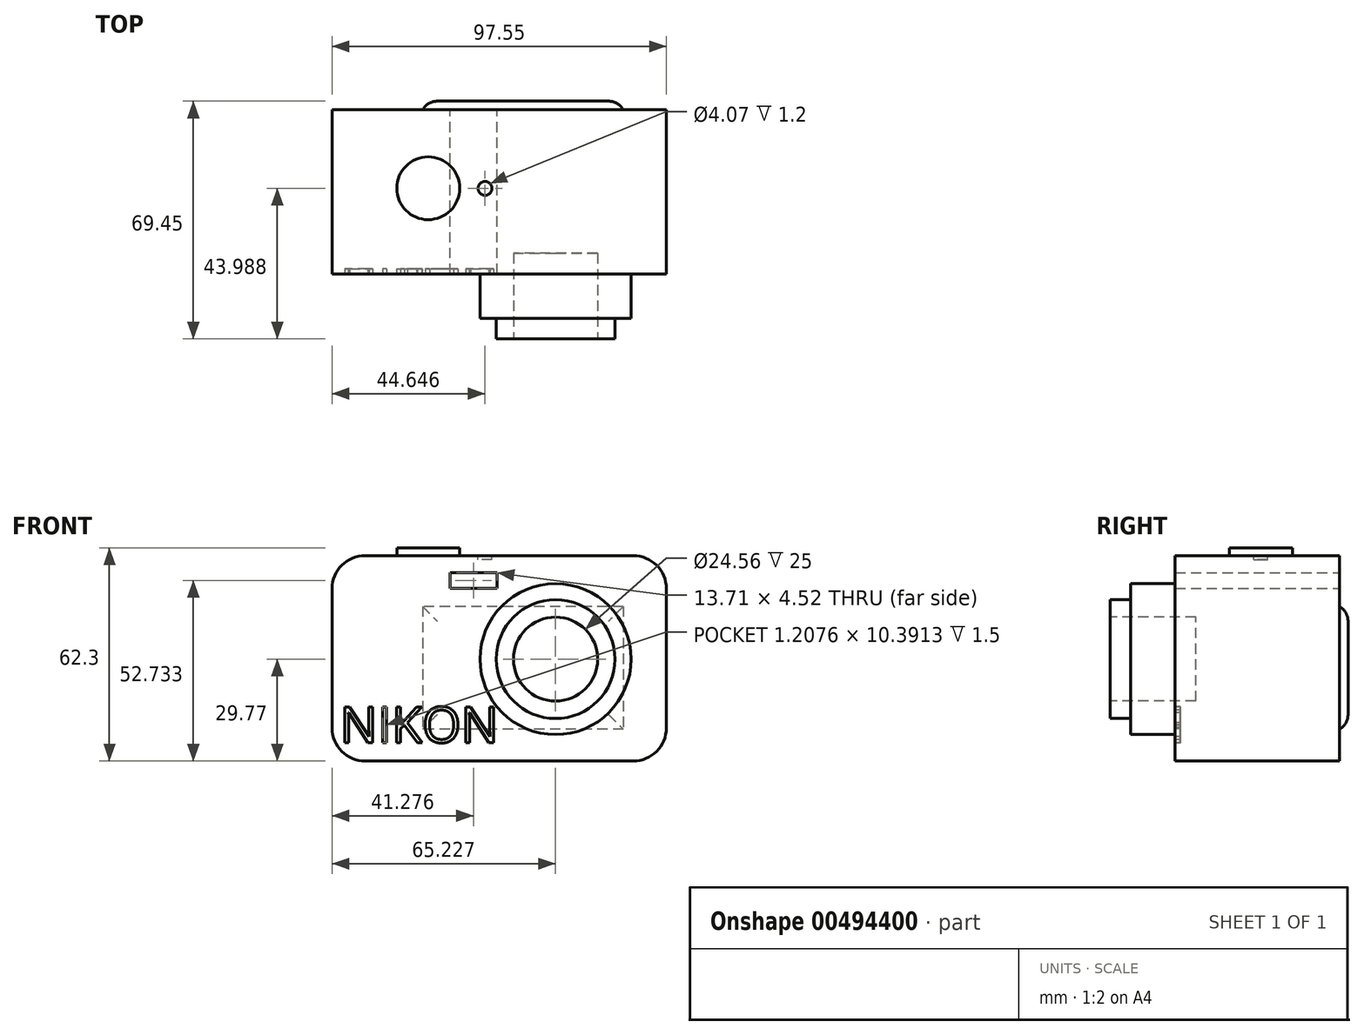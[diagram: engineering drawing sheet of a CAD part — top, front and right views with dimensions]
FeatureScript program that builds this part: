
annotation { "Feature Type Name" : "Feature", "Feature Type Description" : "" }
export const myFeature = defineFeature(function(context is Context, id is Id, definition is map)
    precondition{}
    {
        {
            var Q0;
            Q0=qCreatedBy(makeId("Top.planeOp"),FACE);
            var sketch = newSketch(context, id + "F0", { "sketchPlane" : qUnion([Q0])});
            skLineSegment(sketch, "E0.bottom", {"start": v(-58.63, 22.98) * mm, "end": v(38.92, 22.98) * mm});
            skLineSegment(sketch, "E0.top", {"start": v(-58.63, -24.97) * mm, "end": v(38.92, -24.97) * mm});
            skLineSegment(sketch, "E0.left", {"start": v(-58.63, 22.98) * mm, "end": v(-58.63, -24.97) * mm});
            skLineSegment(sketch, "E0.right", {"start": v(38.92, 22.98) * mm, "end": v(38.92, -24.97) * mm});
            skSolve(sketch);
        }
        {
            var Q0;
            Q0 = qSketchRegion(id + "F0", true);
            extrude(context, id + "F1", {"entities" : qUnion([Q0]), "depth" : 60 * mm});
        }
        {
            var Q0;
            Q0=makeQuery(id+"F1.opExtrude","CAP_EDGE",EDGE,{"disambiguationData":[OSD([sQuery(id+"F0.wireOp",EDGE,"E0.right")])],"isStart":false});
            var Q1;
            Q1=makeQuery(id+"F1.opExtrude","CAP_EDGE",EDGE,{"disambiguationData":[OSD([sQuery(id+"F0.wireOp",EDGE,"E0.left")])],"isStart":false});
            var Q2;
            Q2=makeQuery(id+"F1.opExtrude","CAP_EDGE",EDGE,{"disambiguationData":[OSD([sQuery(id+"F0.wireOp",EDGE,"E0.right")])],"isStart":true});
            var Q3;
            Q3=makeQuery(id+"F1.opExtrude","CAP_EDGE",EDGE,{"disambiguationData":[OSD([sQuery(id+"F0.wireOp",EDGE,"E0.left")])],"isStart":true});
            fillet(context, id + "F2", {"entities" : qUnion([Q0, Q1, Q2, Q3]), "radius" : 9.66 * mm, "tangentPropagation" : true, "allowEdgeOverflow" : false});
        }
        {
            var Q0;
            Q0=makeQuery(id+"F1.opExtrude","SWEPT_FACE",FACE,{"disambiguationData":[OSD([sQuery(id+"F0.wireOp",EDGE,"E0.top")])]});
            var sketch = newSketch(context, id + "F3", { "sketchPlane" : qUnion([Q0])});
            skCircle(sketch, "E1", {"center": v(6.6, 29.77) * mm, "radius": 22.06 * mm});
            skSolve(sketch);
        }
        {
            var Q0;
            Q0 = qSketchRegion(id + "F3", true);
            extrude(context, id + "F4", {"entities" : qUnion([Q0]), "operationType" : NewBodyOperationType.ADD, "depth" : 13 * mm});
        }
        {
            var Q0;
            Q0=makeQuery(id+"F4.opExtrude","CAP_FACE",FACE,{"disambiguationData":[OSD([sQuery(id+"F3.wireOp",EDGE,"E1")])],"isStart":false});
            var sketch = newSketch(context, id + "F5", { "sketchPlane" : qUnion([Q0])});
            skCircle(sketch, "E2", {"center": v(6.6, 29.77) * mm, "radius": 17.35 * mm});
            skSolve(sketch);
        }
        {
            var Q0;
            Q0 = qSketchRegion(id + "F5", true);
            extrude(context, id + "F6", {"entities" : qUnion([Q0]), "operationType" : NewBodyOperationType.ADD, "depth" : 6 * mm});
        }
        {
            var Q0;
            Q0=makeQuery(id+"F6.opExtrude","CAP_FACE",FACE,{"disambiguationData":[OSD([sQuery(id+"F5.wireOp",EDGE,"E2")])],"isStart":false});
            var sketch = newSketch(context, id + "F7", { "sketchPlane" : qUnion([Q0])});
            skCircle(sketch, "E3", {"center": v(6.6, 29.77) * mm, "radius": 12.28 * mm});
            skSolve(sketch);
        }
        {
            var Q0;
            Q0 = qSketchRegion(id + "F7", true);
            extrude(context, id + "F8", {"entities" : qUnion([Q0]), "operationType" : NewBodyOperationType.REMOVE, "oppositeDirection" : true, "depth" : 25 * mm});
        }
        {
            var Q0;
            Q0=makeQuery(id+"F1.opExtrude","CAP_FACE",FACE,{"disambiguationData":[OSD([sQuery(id+"F0.wireOp",EDGE,"E0.bottom"),sQuery(id+"F0.wireOp",EDGE,"E0.top"),sQuery(id+"F0.wireOp",EDGE,"E0.left"),sQuery(id+"F0.wireOp",EDGE,"E0.right")])],"isStart":false});
            var sketch = newSketch(context, id + "F9", { "sketchPlane" : qUnion([Q0])});
            skCircle(sketch, "E4", {"center": v(-30.56, 0.05) * mm, "radius": 9.18 * mm});
            skSolve(sketch);
        }
        {
            var Q0;
            Q0 = qSketchRegion(id + "F9", true);
            extrude(context, id + "F10", {"entities" : qUnion([Q0]), "operationType" : NewBodyOperationType.ADD, "depth" : 2.3 * mm});
        }
        {
            var Q0;
            Q0=makeQuery(id+"F1.opExtrude","CAP_FACE",FACE,{"disambiguationData":[OSD([sQuery(id+"F0.wireOp",EDGE,"E0.bottom"),sQuery(id+"F0.wireOp",EDGE,"E0.top"),sQuery(id+"F0.wireOp",EDGE,"E0.left"),sQuery(id+"F0.wireOp",EDGE,"E0.right")])],"isStart":false});
            var sketch = newSketch(context, id + "F11", { "sketchPlane" : qUnion([Q0])});
            skCircle(sketch, "E5", {"center": v(-13.98, 0.02) * mm, "radius": 2.03 * mm});
            skSolve(sketch);
        }
        {
            var Q0;
            Q0 = qSketchRegion(id + "F11", true);
            extrude(context, id + "F12", {"entities" : qUnion([Q0]), "operationType" : NewBodyOperationType.REMOVE, "oppositeDirection" : true, "depth" : 1.2 * mm});
        }
        {
            var Q0;
            Q0=makeQuery(id+"F1.opExtrude","SWEPT_FACE",FACE,{"disambiguationData":[OSD([sQuery(id+"F0.wireOp",EDGE,"E0.bottom")])]});
            var sketch = newSketch(context, id + "F13", { "sketchPlane" : qUnion([Q0])});
            skLineSegment(sketch, "E6.bottom", {"start": v(10.5, 55) * mm, "end": v(24.2, 55) * mm});
            skLineSegment(sketch, "E6.top", {"start": v(10.5, 50.47) * mm, "end": v(24.2, 50.47) * mm});
            skLineSegment(sketch, "E6.left", {"start": v(10.5, 55) * mm, "end": v(10.5, 50.47) * mm});
            skLineSegment(sketch, "E6.right", {"start": v(24.2, 55) * mm, "end": v(24.2, 50.47) * mm});
            skSolve(sketch);
        }
        {
            var Q0;
            Q0 = qSketchRegion(id + "F13", true);
            extrude(context, id + "F14", {"entities" : qUnion([Q0]), "operationType" : NewBodyOperationType.REMOVE, "oppositeDirection" : true, "depth" : 69.5 * mm});
        }
        {
            var Q0;
            Q0=makeQuery(id+"F1.opExtrude","SWEPT_FACE",FACE,{"disambiguationData":[OSD([sQuery(id+"F0.wireOp",EDGE,"E0.bottom")])]});
            var sketch = newSketch(context, id + "F15", { "sketchPlane" : qUnion([Q0])});
            skLineSegment(sketch, "E7.bottom", {"start": v(-26.37, 45.16) * mm, "end": v(32.23, 45.16) * mm});
            skLineSegment(sketch, "E7.top", {"start": v(-26.37, 9.26) * mm, "end": v(32.23, 9.26) * mm});
            skLineSegment(sketch, "E7.left", {"start": v(-26.37, 45.16) * mm, "end": v(-26.37, 9.26) * mm});
            skLineSegment(sketch, "E7.right", {"start": v(32.23, 45.16) * mm, "end": v(32.23, 9.26) * mm});
            skSolve(sketch);
        }
        {
            var Q0;
            Q0=makeQuery(id+"F15.imprint","IMPRINT",FACE,{"disambiguationData":[TD([[makeQuery(id+"F15.imprint","IMPRINT",EDGE,{"derivedFrom":sQuery(id+"F15.wireOp",EDGE,"E7.bottom")}),-1.0]])]});
            extrude(context, id + "F16", {"entities" : qUnion([Q0]), "operationType" : NewBodyOperationType.ADD, "depth" : 2.5 * mm});
        }
        {
            var Q0;
            Q0=makeQuery(id+"F16.opExtrude","CAP_FACE",FACE,{"disambiguationData":[OSD([sQuery(id+"F15.wireOp",EDGE,"E7.bottom"),sQuery(id+"F15.wireOp",EDGE,"E7.top"),sQuery(id+"F15.wireOp",EDGE,"E7.left"),sQuery(id+"F15.wireOp",EDGE,"E7.right")])],"isStart":false});
            fillet(context, id + "F17", {"entities" : qUnion([Q0]), "radius" : 5 * mm, "tangentPropagation" : true, "allowEdgeOverflow" : false});
        }
        {
            var Q0;
            Q0=makeQuery(id+"F1.opExtrude","SWEPT_FACE",FACE,{"disambiguationData":[OSD([sQuery(id+"F0.wireOp",EDGE,"E0.top")])]});
            var sketch = newSketch(context, id + "F18", { "sketchPlane" : qUnion([Q0])});
            skText(sketch, "E8", { "text": "NIKON", "fontName": "OpenSans-Regular.ttf"});
            const initialGuessF18  = {"E8": [-0.05631, 0.00538, 1, 0, 0.01048]};
            skSetInitialGuess(sketch, initialGuessF18);
            skSolve(sketch);
        }
        {
            var Q0;
            Q0 = qSketchRegion(id + "F18", true);
            extrude(context, id + "F19", {"entities" : qUnion([Q0]), "operationType" : NewBodyOperationType.REMOVE, "oppositeDirection" : true, "depth" : 1.5 * mm});
        }
    });
